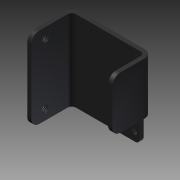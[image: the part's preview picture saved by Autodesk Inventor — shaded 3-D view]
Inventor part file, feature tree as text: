
AUTODESK INVENTOR PART (.ipt)
format: ipt  version: 2015 (Build 190159000, 159)  size: 194,048 bytes
history: native  units: mm
features: extrude x3, fillet x2, hole x2, other x2
ambient origin geometry x8: Origin, YZ Plane, XZ Plane, XY Plane, X Axis, Y Axis, Z Axis, Center Point
bodies: Solid1 (feature_tree)
feature tree (9):
  extrude  "Extrusión1"  Depth=2.0mm
  fillet  "Empalme1"  Radius=2.0mm
  extrude  "Extrusión2"  Depth=2.0mm
  hole  "Agujero1"  [1 undecoded]
  hole  "Agujero2"  [1 undecoded]
  extrude  "Extrusión3"  Depth=20.0mm
  other  "Desplazar cara1"
  fillet  "Empalme2"  Radius=40.0mm
  other  "Definición1"
note: 2 required parameter values undecoded (feature->parameter linkage not recoverable at this tier; creation-order binding heuristic only, values carry confidence <= 0.55)
